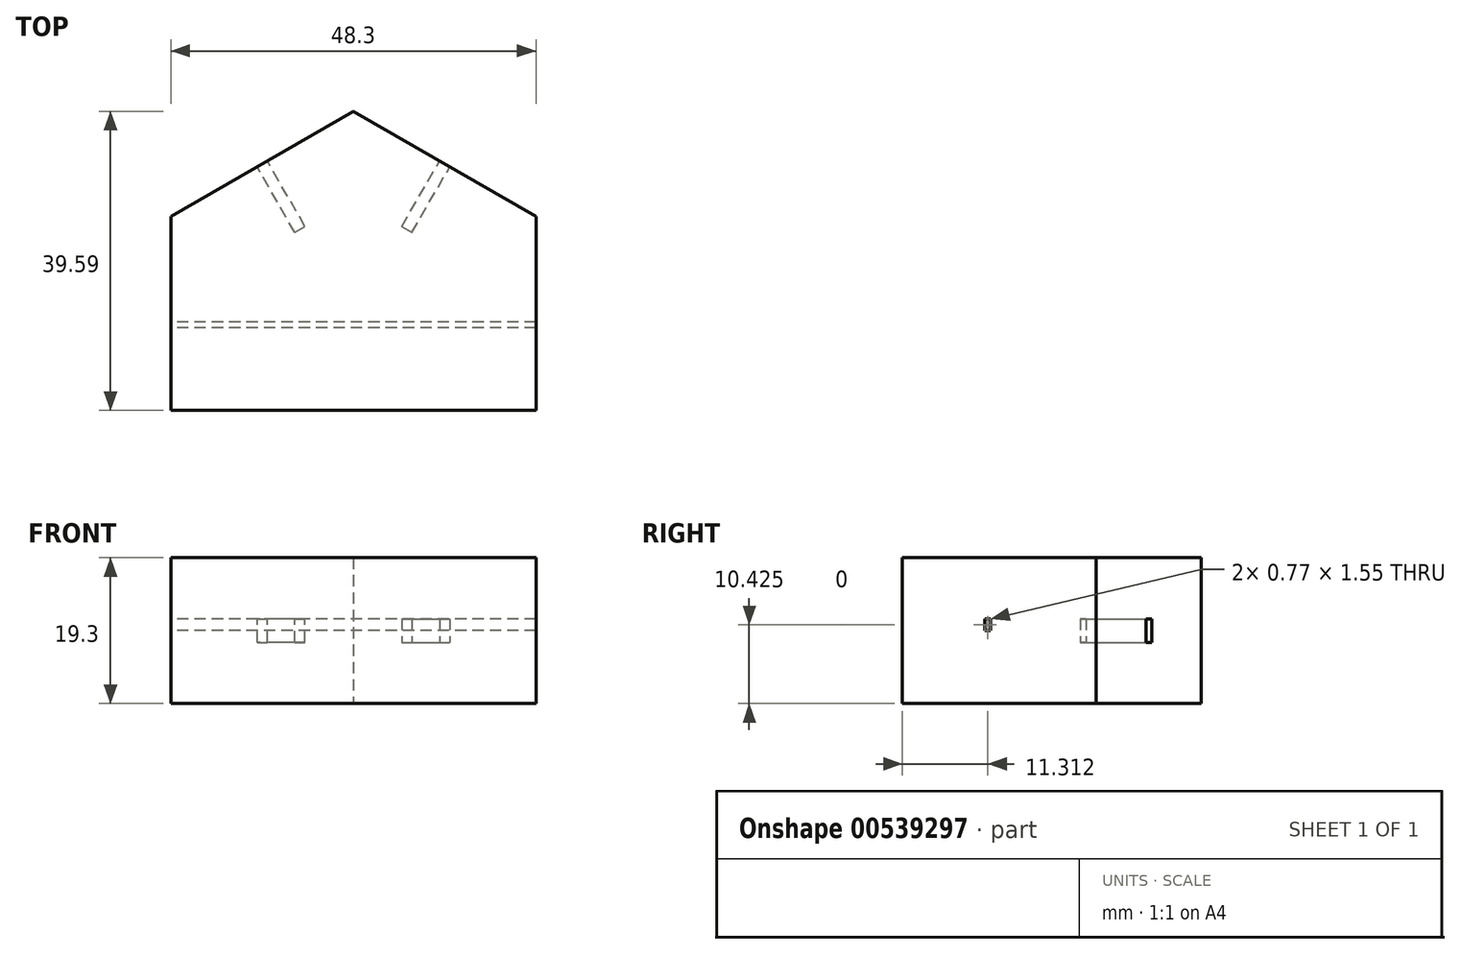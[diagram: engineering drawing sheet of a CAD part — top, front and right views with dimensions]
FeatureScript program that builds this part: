
annotation { "Feature Type Name" : "Feature", "Feature Type Description" : "" }
export const myFeature = defineFeature(function(context is Context, id is Id, definition is map)
    precondition{}
    {
        {
            var Q0;
            Q0=qCreatedBy(makeId("Top.planeOp"),FACE);
            var sketch = newSketch(context, id + "F0", { "sketchPlane" : qUnion([Q0])});
            skLineSegment(sketch, "E0", {"start": v(0, 0) * mm, "end": v(-24.15, 0) * mm});
            skLineSegment(sketch, "E1", {"start": v(-24.15, 0) * mm, "end": v(-24.15, 25.64) * mm});
            skLineSegment(sketch, "E2", {"start": v(-24.15, 11.7) * mm, "end": v(0, 11.7) * mm});
            skLineSegment(sketch, "E3", {"start": v(0, 0) * mm, "end": v(0, 11.7) * mm});
            skLineSegment(sketch, "E4", {"start": v(0, 11.7) * mm, "end": v(-12.08, 32.61) * mm});
            skLineSegment(sketch, "E5", {"start": v(0, 39.59) * mm, "end": v(-24.15, 25.64) * mm});
            skLineSegment(sketch, "E6.MirrorCS", {"start": v(0, 0) * mm, "end": v(24.15, 0) * mm});
            skLineSegment(sketch, "E7.MirrorCS", {"start": v(24.15, 11.7) * mm, "end": v(0, 11.7) * mm});
            skLineSegment(sketch, "E8.MirrorCS", {"start": v(0, 11.7) * mm, "end": v(12.08, 32.61) * mm});
            skLineSegment(sketch, "E9.MirrorCS", {"start": v(0, 39.59) * mm, "end": v(24.15, 25.64) * mm});
            skLineSegment(sketch, "E10.MirrorCS", {"start": v(24.15, 0) * mm, "end": v(24.15, 25.64) * mm});
            skSolve(sketch);
        }
        {
            var Q0;
            {var subQ3=sQuery(id+"F0.wireOp",EDGE,"E2");Q0=makeQuery(id+"F0.imprint","IMPRINT",FACE,{"disambiguationData":[TD([[makeQuery(id+"F0.imprint","IMPRINT",EDGE,{"derivedFrom":subQ3}),1.0]])]});}
            var Q1;
            {var subQ0=sQuery(id+"F0.wireOp",EDGE,"E0");Q1=makeQuery(id+"F0.imprint","IMPRINT",FACE,{"disambiguationData":[TD([[makeQuery(id+"F0.imprint","IMPRINT",EDGE,{"derivedFrom":subQ0}),-1.0]])]});}
            var Q2;
            Q2=makeQuery(id+"F0.imprint","IMPRINT",FACE,{"disambiguationData":[TD([[makeQuery(id+"F0.imprint","IMPRINT",EDGE,{"derivedFrom":sQuery(id+"F0.wireOp",EDGE,"E3")}),-1.0]])]});
            var Q3;
            {var subQ0=sQuery(id+"F0.wireOp",EDGE,"E7.MirrorCS");Q3=makeQuery(id+"F0.imprint","IMPRINT",FACE,{"disambiguationData":[TD([[makeQuery(id+"F0.imprint","IMPRINT",EDGE,{"derivedFrom":subQ0}),-1.0]])]});}
            var Q4;
            {var subQ0=sQuery(id+"F0.wireOp",EDGE,"E4");Q4=makeQuery(id+"F0.imprint","IMPRINT",FACE,{"disambiguationData":[TD([[makeQuery(id+"F0.imprint","IMPRINT",EDGE,{"derivedFrom":subQ0}),-1.0]])]});}
            extrude(context, id + "F1", {"entities" : qUnion([Q0, Q1, Q2, Q3, Q4]), "endBound" : BoundingType.SYMMETRIC, "depth" : 19.3 * mm, "offsetDistance" : 25 * mm});
        }
        {
            var Q0;
            Q0=makeQuery(id+"F1.opExtrude","SWEPT_FACE",FACE,{"disambiguationData":[OSD([sQuery(id+"F0.wireOp",EDGE,"E1")])]});
            var sketch = newSketch(context, id + "F2", { "sketchPlane" : qUnion([Q0])});
            skLineSegment(sketch, "E11", {"start": v(0, 0) * mm, "end": v(-11.7, 0) * mm});
            skPoint(sketch, "E11.endSnap0", {"position": v(0, 0) * mm});
            skLineSegment(sketch, "E12.bottom", {"start": v(-12.47, 1.55) * mm, "end": v(-10.93, 1.55) * mm});
            skLineSegment(sketch, "E12.top", {"start": v(-12.47, -1.55) * mm, "end": v(-10.93, -1.55) * mm});
            skLineSegment(sketch, "E12.left", {"start": v(-12.47, 1.55) * mm, "end": v(-12.47, -1.55) * mm});
            skLineSegment(sketch, "E12.right", {"start": v(-10.92, 1.55) * mm, "end": v(-10.93, -1.55) * mm});
            skPoint(sketch, "E12.middle", {"position": v(-11.7, 0) * mm});
            skLineSegment(sketch, "E13", {"start": v(-11.7, 1.55) * mm, "end": v(-11.7, -1.55) * mm});
            skSolve(sketch);
        }
        {
            var Q0;
            {var subQ1=sQuery(id+"F2.wireOp",EDGE,"E12.bottom");Q0=makeQuery(id+"F2.imprint","IMPRINT",FACE,{"disambiguationData":[TD([[makeQuery(id+"F2.imprint","IMPRINT",EDGE,{"derivedFrom":subQ1}),-1.0]])]});}
            extrude(context, id + "F3", {"entities" : qUnion([Q0]), "operationType" : NewBodyOperationType.REMOVE, "oppositeDirection" : true, "depth" : 48.3 * mm, "offsetDistance" : 25 * mm});
        }
        {
            var Q0;
            Q0=makeQuery(id+"F1.opExtrude","SWEPT_FACE",FACE,{"disambiguationData":[OSD([sQuery(id+"F0.wireOp",EDGE,"E9.MirrorCS")])]});
            var sketch = newSketch(context, id + "F4", { "sketchPlane" : qUnion([Q0])});
            skLineSegment(sketch, "E14", {"start": v(19.8, 0) * mm, "end": v(-8.1, 0) * mm});
            skLineSegment(sketch, "E15.bottom", {"start": v(6.63, 1.55) * mm, "end": v(5.08, 1.55) * mm});
            skLineSegment(sketch, "E15.top", {"start": v(6.63, -1.55) * mm, "end": v(5.08, -1.55) * mm});
            skLineSegment(sketch, "E15.left", {"start": v(6.63, 1.55) * mm, "end": v(6.63, -1.55) * mm});
            skLineSegment(sketch, "E15.right", {"start": v(5.08, 1.55) * mm, "end": v(5.08, -1.55) * mm});
            skPoint(sketch, "E15.middle", {"position": v(5.85, 0) * mm});
            skSolve(sketch);
        }
        {
            var Q0;
            {var subQ5=sQuery(id+"F4.wireOp",EDGE,"E15.bottom");Q0=makeQuery(id+"F4.imprint","IMPRINT",FACE,{"disambiguationData":[TD([[makeQuery(id+"F4.imprint","IMPRINT",EDGE,{"derivedFrom":subQ5}),1.0]])]});}
            var Q1;
            {var subQ5=sQuery(id+"F4.wireOp",EDGE,"E15.top");Q1=makeQuery(id+"F4.imprint","IMPRINT",FACE,{"disambiguationData":[TD([[makeQuery(id+"F4.imprint","IMPRINT",EDGE,{"derivedFrom":subQ5}),-1.0]])]});}
            extrude(context, id + "F5", {"entities" : qUnion([Q0, Q1]), "operationType" : NewBodyOperationType.REMOVE, "oppositeDirection" : true, "depth" : 10 * mm, "offsetDistance" : 25 * mm});
        }
        {
            var Q0;
            Q0=makeQuery(id+"F1.opExtrude","SWEPT_FACE",FACE,{"disambiguationData":[OSD([sQuery(id+"F0.wireOp",EDGE,"E5")])]});
            var sketch = newSketch(context, id + "F6", { "sketchPlane" : qUnion([Q0])});
            skLineSegment(sketch, "E16", {"start": v(8.1, 0) * mm, "end": v(-19.8, 0) * mm});
            skLineSegment(sketch, "E17.bottom", {"start": v(-5.08, -1.55) * mm, "end": v(-6.63, -1.55) * mm});
            skLineSegment(sketch, "E17.top", {"start": v(-5.08, 1.55) * mm, "end": v(-6.63, 1.55) * mm});
            skLineSegment(sketch, "E17.left", {"start": v(-5.08, -1.55) * mm, "end": v(-5.08, 1.55) * mm});
            skLineSegment(sketch, "E17.right", {"start": v(-6.63, -1.55) * mm, "end": v(-6.63, 1.55) * mm});
            skPoint(sketch, "E17.middle", {"position": v(-5.85, 0) * mm});
            skSolve(sketch);
        }
        {
            var Q0;
            {var subQ5=sQuery(id+"F6.wireOp",EDGE,"E17.bottom");Q0=makeQuery(id+"F6.imprint","IMPRINT",FACE,{"disambiguationData":[TD([[makeQuery(id+"F6.imprint","IMPRINT",EDGE,{"derivedFrom":subQ5}),-1.0]])]});}
            var Q1;
            {var subQ5=sQuery(id+"F6.wireOp",EDGE,"E17.top");Q1=makeQuery(id+"F6.imprint","IMPRINT",FACE,{"disambiguationData":[TD([[makeQuery(id+"F6.imprint","IMPRINT",EDGE,{"derivedFrom":subQ5}),1.0]])]});}
            extrude(context, id + "F7", {"entities" : qUnion([Q0, Q1]), "operationType" : NewBodyOperationType.REMOVE, "oppositeDirection" : true, "depth" : 10 * mm, "offsetDistance" : 25 * mm});
        }
    });
